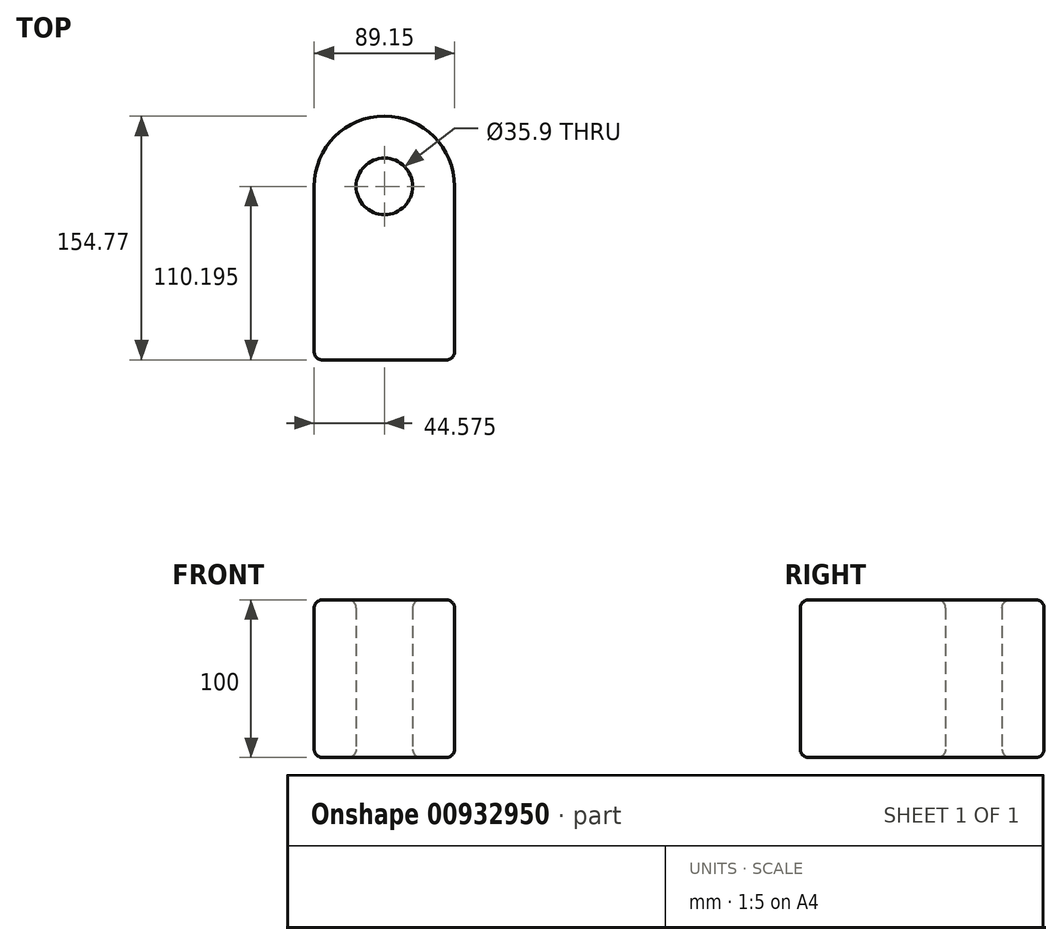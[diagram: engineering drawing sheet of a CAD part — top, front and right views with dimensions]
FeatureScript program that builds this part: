
annotation { "Feature Type Name" : "Feature", "Feature Type Description" : "" }
export const myFeature = defineFeature(function(context is Context, id is Id, definition is map)
    precondition{}
    {
        {
            var Q0;
            Q0=qCreatedBy(makeId("Top.planeOp"),FACE);
            var sketch = newSketch(context, id + "F0", { "sketchPlane" : qUnion([Q0])});
            skLineSegment(sketch, "E0", {"start": v(-52.4, 35.84) * mm, "end": v(-52.4, -74.35) * mm});
            skLineSegment(sketch, "E1", {"start": v(-52.4, -74.35) * mm, "end": v(36.75, -74.35) * mm});
            skLineSegment(sketch, "E2", {"start": v(36.75, -74.35) * mm, "end": v(36.75, 35.84) * mm});
            skCircle(sketch, "E3", {"center": v(-7.83, 35.84) * mm, "radius": 17.95 * mm});
            skPoint(sketch, "E3.centerSnap0", {"position": v(-7.83, -74.35) * mm});
            skArc(sketch, "E4", {"start": v(36.75, 35.84) * mm, "mid": v(-7.83, 80.42) * mm, "end": v(-52.4, 35.84) * mm});
            skSolve(sketch);
        }
        {
            var Q0;
            Q0 = qSketchRegion(id + "F0", true);
            extrude(context, id + "F1", {"entities" : qUnion([Q0]), "depth" : 100 * mm, "offsetDistance" : 25 * mm});
        }
        {
            var Q0;
            Q0=makeQuery(id+"F1.opExtrude","CAP_EDGE",EDGE,{"disambiguationData":[OSD([sQuery(id+"F0.wireOp",EDGE,"E4")])],"isStart":true});
            var Q1;
            Q1=makeQuery(id+"F1.opExtrude","CAP_EDGE",EDGE,{"disambiguationData":[OSD([sQuery(id+"F0.wireOp",EDGE,"E2")])],"isStart":false});
            var Q2;
            Q2=makeQuery(id+"F1.opExtrude","CAP_EDGE",EDGE,{"disambiguationData":[OSD([sQuery(id+"F0.wireOp",EDGE,"E4")])],"isStart":false});
            var Q3;
            Q3=makeQuery(id+"F1.opExtrude","SWEPT_EDGE",EDGE,{"disambiguationData":[OSD([sQuery(id+"F0.wireOp",EDGE,"E1"),sQuery(id+"F0.wireOp",EDGE,"E2")])]});
            var Q4;
            Q4=makeQuery(id+"F1.opExtrude","CAP_EDGE",EDGE,{"disambiguationData":[OSD([sQuery(id+"F0.wireOp",EDGE,"E0")])],"isStart":false});
            var Q5;
            Q5=makeQuery(id+"F1.opExtrude","CAP_EDGE",EDGE,{"disambiguationData":[OSD([sQuery(id+"F0.wireOp",EDGE,"E0")])],"isStart":true});
            var Q6;
            Q6=makeQuery(id+"F1.opExtrude","CAP_EDGE",EDGE,{"disambiguationData":[OSD([sQuery(id+"F0.wireOp",EDGE,"E1")])],"isStart":true});
            var Q7;
            Q7=makeQuery(id+"F1.opExtrude","SWEPT_EDGE",EDGE,{"disambiguationData":[OSD([sQuery(id+"F0.wireOp",EDGE,"E0"),sQuery(id+"F0.wireOp",EDGE,"E1")])]});
            var Q8;
            Q8=makeQuery(id+"F1.opExtrude","CAP_EDGE",EDGE,{"disambiguationData":[OSD([sQuery(id+"F0.wireOp",EDGE,"E1")])],"isStart":false});
            var Q9;
            Q9=makeQuery(id+"F1.opExtrude","CAP_EDGE",EDGE,{"disambiguationData":[OSD([sQuery(id+"F0.wireOp",EDGE,"E2")])],"isStart":true});
            fillet(context, id + "F2", {"entities" : qUnion([Q0, Q1, Q2, Q3, Q4, Q5, Q6, Q7, Q8, Q9]), "radius" : 5 * mm, "tangentPropagation" : true, "allowEdgeOverflow" : false});
        }
        {
            var Q0;
            Q0=makeQuery(id+"F1.opExtrude","CAP_EDGE",EDGE,{"disambiguationData":[OSD([sQuery(id+"F0.wireOp",EDGE,"E3")])],"isStart":false});
            var Q1;
            Q1=makeQuery(id+"F1.opExtrude","CAP_EDGE",EDGE,{"disambiguationData":[OSD([sQuery(id+"F0.wireOp",EDGE,"E3")])],"isStart":true});
            fillet(context, id + "F3", {"entities" : qUnion([Q0, Q1]), "radius" : 5 * mm, "tangentPropagation" : true, "allowEdgeOverflow" : false});
        }
    });
